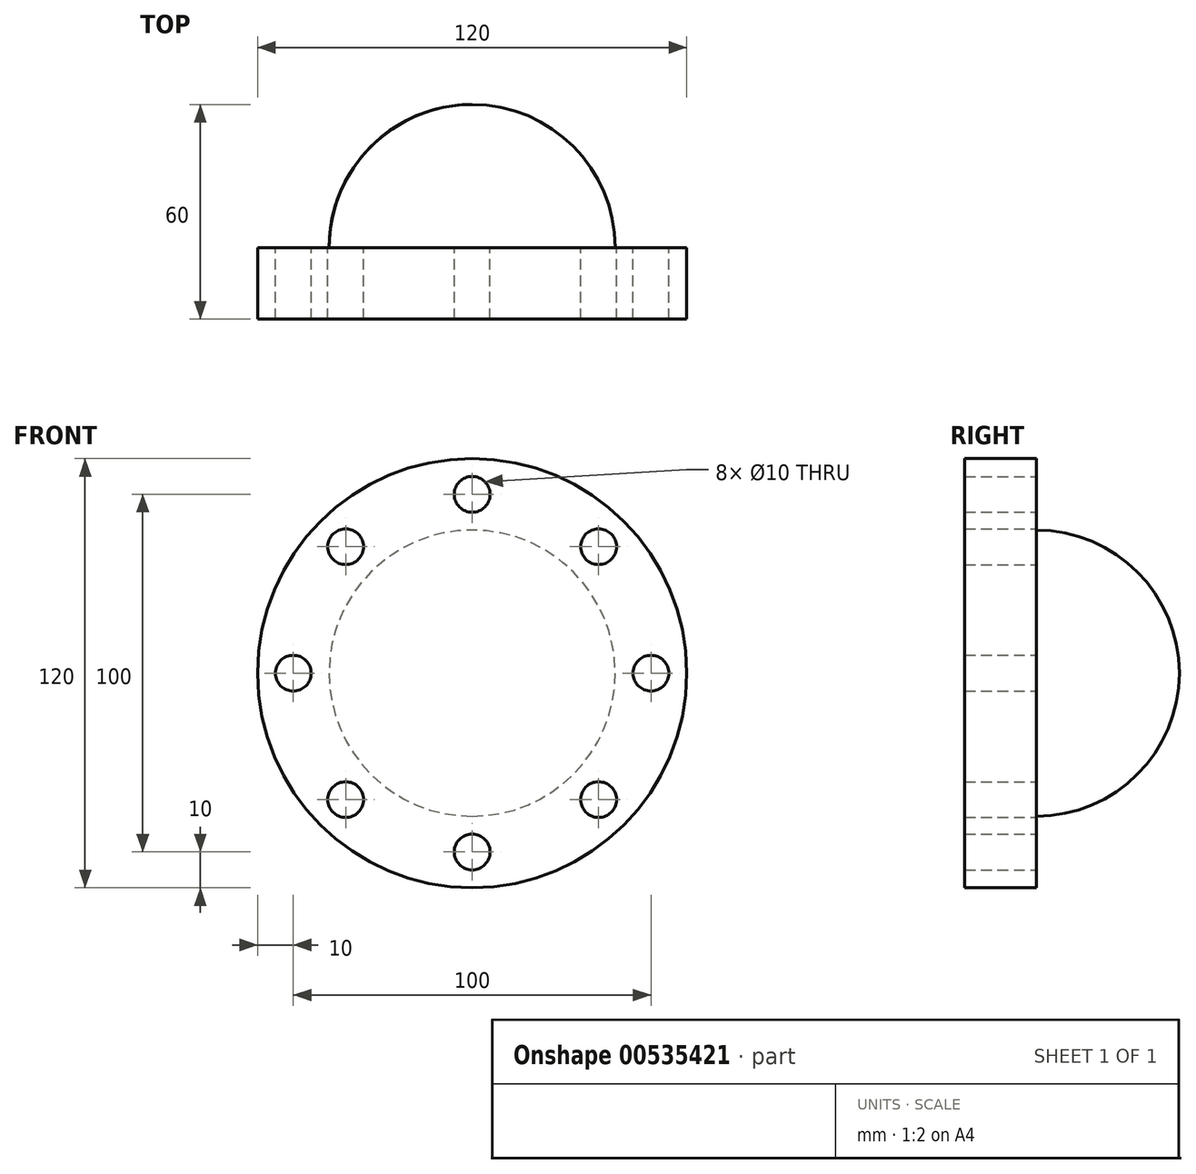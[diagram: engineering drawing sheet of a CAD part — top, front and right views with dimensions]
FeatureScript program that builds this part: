
annotation { "Feature Type Name" : "Feature", "Feature Type Description" : "" }
export const myFeature = defineFeature(function(context is Context, id is Id, definition is map)
    precondition{}
    {
        {
            var Q0;
            Q0=qCreatedBy(makeId("Front.planeOp"),FACE);
            var sketch = newSketch(context, id + "F0", { "sketchPlane" : qUnion([Q0])});
            skCircle(sketch, "E0", {"center": v(0, 0) * mm, "radius": 60 * mm});
            skCircle(sketch, "E1", {"center": v(0, 50) * mm, "radius": 5 * mm});
            skCircle(sketch, "E2.1.0", {"center": v(-35.36, 35.36) * mm, "radius": 5 * mm});
            skCircle(sketch, "E2.2.0", {"center": v(-50, 0) * mm, "radius": 5 * mm});
            skCircle(sketch, "E2.3.0", {"center": v(-35.36, -35.36) * mm, "radius": 5 * mm});
            skCircle(sketch, "E2.4.0", {"center": v(0, -50) * mm, "radius": 5 * mm});
            skCircle(sketch, "E2.5.0", {"center": v(35.36, -35.36) * mm, "radius": 5 * mm});
            skCircle(sketch, "E2.6.0", {"center": v(50, 0) * mm, "radius": 5 * mm});
            skCircle(sketch, "E2.7.0", {"center": v(35.36, 35.36) * mm, "radius": 5 * mm});
            skSolve(sketch);
        }
        {
            var Q0;
            Q0 = qSketchRegion(id + "F0", true);
            extrude(context, id + "F1", {"entities" : qUnion([Q0]), "depth" : 20 * mm, "offsetDistance" : 25 * mm});
        }
        {
            var Q0;
            Q0=qCreatedBy(makeId("Top.planeOp"),FACE);
            var sketch = newSketch(context, id + "F2", { "sketchPlane" : qUnion([Q0])});
            skLineSegment(sketch, "E3", {"start": v(60, 0) * mm, "end": v(60, -20) * mm});
            skLineSegment(sketch, "E4", {"start": v(-60, -20) * mm, "end": v(-60, 0) * mm});
            skArc(sketch, "E5", {"start": v(0, 40) * mm, "mid": v(-28.28, 28.28) * mm, "end": v(-40, 0) * mm});
            skLineSegment(sketch, "E6", {"start": v(0, 0) * mm, "end": v(0, 40) * mm});
            skLineSegment(sketch, "E7.0", {"start": v(0, 0) * mm, "end": v(-40, 0) * mm});
            skPoint(sketch, "E8.orphan", {"position": v(60, 0) * mm});
            skPoint(sketch, "E9.orphan", {"position": v(-60, 0) * mm});
            skSolve(sketch);
        }
        {
            var Q0;
            Q0=makeQuery(id+"F2.imprint","IMPRINT",FACE,{"disambiguationData":[TD([[makeQuery(id+"F2.imprint","IMPRINT",EDGE,{"derivedFrom":sQuery(id+"F2.wireOp",EDGE,"E5")}),1.0]])]});
            var Q1;
            Q1=sQuery(id+"F2.wireOp",EDGE,"E6");
            revolve(context, id + "F3", {"operationType" : NewBodyOperationType.ADD, "entities" : qUnion([Q0]), "axis" : qUnion([Q1]), "revolveType" : RevolveType.FULL});
        }
    });
